# Revit family: Electrical_Equipment-HCS-Emergency_Lighting_Controls-Relay
name_source: partatom
category: Electrical Equipment
revit_build: Autodesk Revit 2014 (Build: 20130308_1515(x64)
units: mm (PartAtom-declared; Revit-internal decimal feet)

## types (1)
- UL924
    Apparent Load = 0.800 VA
    Certifications = UL Listed, UL924
    Connector Description 1 = Direct Current Power Supply
    Connector Description 2 = Controls
    Default Elevation = 0 "
    Description = UL924 Enclosed 20 AMP Emergency Lighting Control Relay
    Flame Rating = UL94V-0
    Frequency = 60 Hz
    Housing Rating = Plenum, NEMA 1
    Humidity = 0% to 90% non condensing 
relative humidity
    Load Classification = Power
    Manufacturer = Hubbell Controls Solution
    Model = UL924
    Number of Poles = 1
    Operating Environment = Indoor use only
    Operating Temperature = 32° to 140°F (0° to 60°C)
    Power Factor = 1
    Product Documentation Link = https://hubbellcdn.com
    Product Material = Hubbell - Black
    Product Page URL = https://www.hubbell.com
    Type Comments = Electrical Equipment
    URL = https://www.hubbell.com
    Voltage = 120V
    Voltage Input = 120 V
    Warranty = Five years
    Wires = 7”, 105° C, 600V Rated

## geometry (parser evidence)
native form markers: Blend x2, Sweep x2
no freeform markers — native parametric forms only
